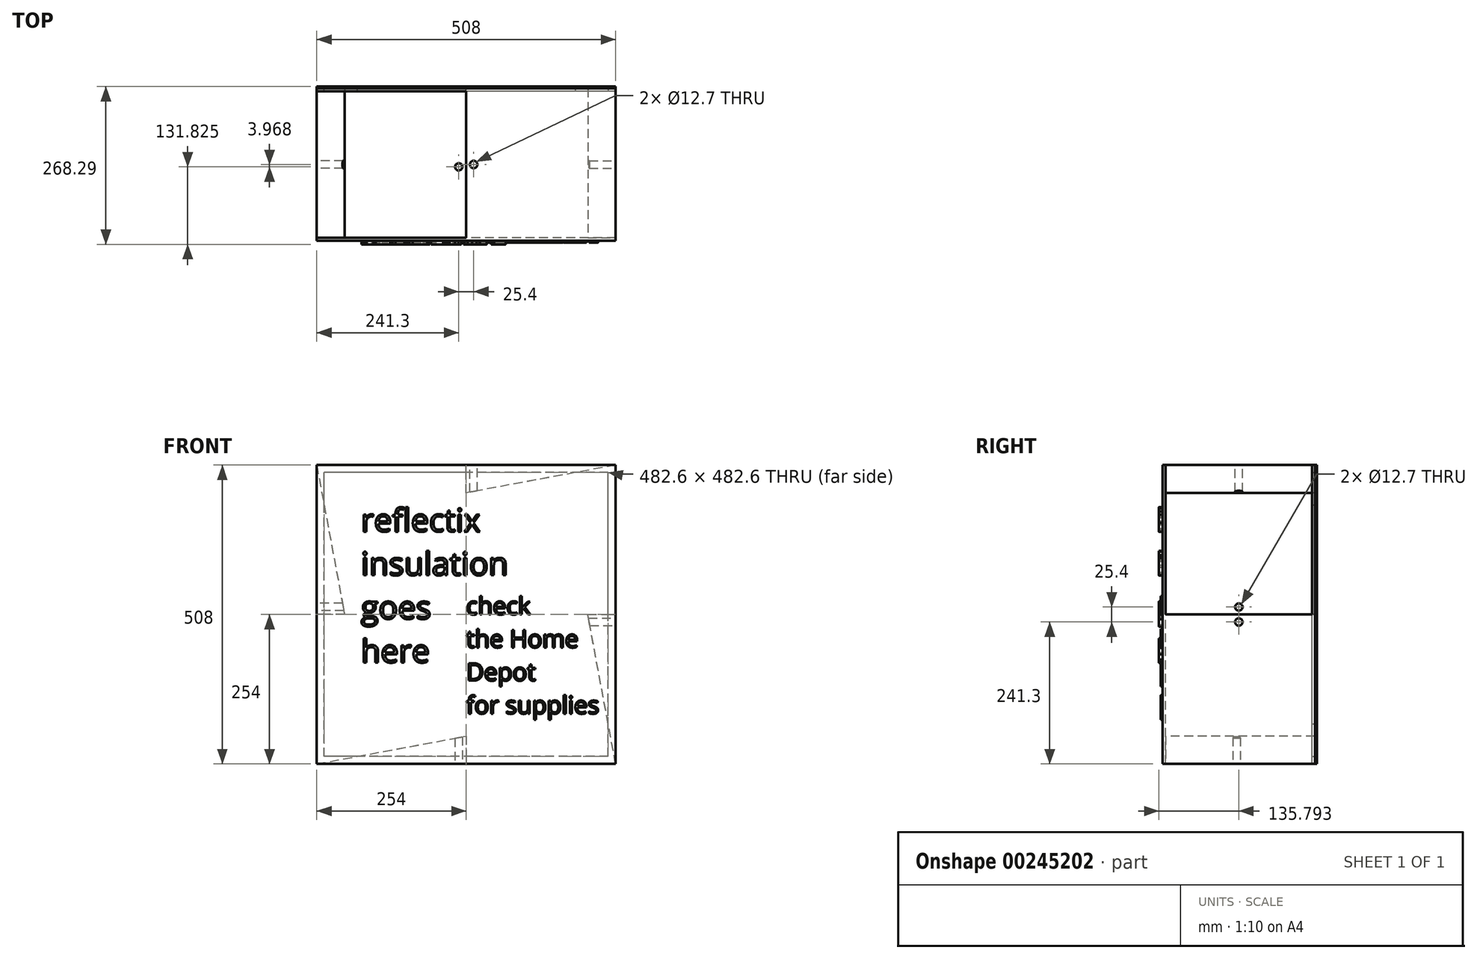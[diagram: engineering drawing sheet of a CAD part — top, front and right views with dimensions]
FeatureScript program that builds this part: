
annotation { "Feature Type Name" : "Feature", "Feature Type Description" : "" }
export const myFeature = defineFeature(function(context is Context, id is Id, definition is map)
    precondition{}
    {
        {
            var Q0;
            Q0=qCreatedBy(makeId("Front.planeOp"),FACE);
            var sketch = newSketch(context, id + "F0", { "sketchPlane" : qUnion([Q0])});
            skLineSegment(sketch, "E0.bottom", {"start": v(254, -254) * mm, "end": v(-254, -254) * mm});
            skLineSegment(sketch, "E0.top", {"start": v(254, 254) * mm, "end": v(-254, 254) * mm});
            skLineSegment(sketch, "E0.left", {"start": v(254, -254) * mm, "end": v(254, 254) * mm});
            skLineSegment(sketch, "E0.right", {"start": v(-254, -254) * mm, "end": v(-254, 254) * mm});
            skPoint(sketch, "E0.middle", {"position": v(0, 0) * mm});
            skSolve(sketch);
        }
        {
            var Q0;
            Q0=makeQuery(id+"F0.imprint","IMPRINT",FACE,{"disambiguationData":[TD([[makeQuery(id+"F0.imprint","IMPRINT",EDGE,{"derivedFrom":sQuery(id+"F0.wireOp",EDGE,"E0.bottom")}),-1.0]])]});
            extrude(context, id + "F1", {"entities" : qUnion([Q0]), "endBound" : BoundingType.SYMMETRIC, "depth" : 4.76 * mm});
        }
        {
            var Q0;
            Q0=makeQuery(id+"F1.opExtrude","CAP_FACE",FACE,{"disambiguationData":[OSD([sQuery(id+"F0.wireOp",EDGE,"E0.bottom"),sQuery(id+"F0.wireOp",EDGE,"E0.top"),sQuery(id+"F0.wireOp",EDGE,"E0.left"),sQuery(id+"F0.wireOp",EDGE,"E0.right")])],"isStart":false});
            var sketch = newSketch(context, id + "F2", { "sketchPlane" : qUnion([Q0])});
            skLineSegment(sketch, "E1", {"start": v(-254, 254) * mm, "end": v(-206.7, 0) * mm});
            skLineSegment(sketch, "E2", {"start": v(-254, -254) * mm, "end": v(0, -206.7) * mm});
            skLineSegment(sketch, "E3", {"start": v(254, -254) * mm, "end": v(206.7, 0) * mm});
            skPoint(sketch, "E3.endSnap0", {"position": v(254, 0) * mm});
            skLineSegment(sketch, "E4", {"start": v(254, 254) * mm, "end": v(0, 206.7) * mm});
            skLineSegment(sketch, "E5", {"start": v(0, 206.7) * mm, "end": v(0, 254) * mm});
            skLineSegment(sketch, "E6", {"start": v(0, 254) * mm, "end": v(254, 254) * mm});
            skLineSegment(sketch, "E7", {"start": v(206.7, 0) * mm, "end": v(254, 0) * mm});
            skLineSegment(sketch, "E8", {"start": v(254, 0) * mm, "end": v(254, -254) * mm});
            skLineSegment(sketch, "E9", {"start": v(0, -206.7) * mm, "end": v(0, -254) * mm});
            skLineSegment(sketch, "E10", {"start": v(0, -254) * mm, "end": v(-254, -254) * mm});
            skLineSegment(sketch, "E11", {"start": v(-206.7, 0) * mm, "end": v(-254, 0) * mm});
            skLineSegment(sketch, "E12", {"start": v(-254, 0) * mm, "end": v(-254, 254) * mm});
            skSolve(sketch);
        }
        {
            var Q0;
            Q0=makeQuery(id+"F2.imprint","IMPRINT",FACE,{"disambiguationData":[TD([[makeQuery(id+"F2.imprint","IMPRINT",EDGE,{"derivedFrom":sQuery(id+"F2.wireOp",EDGE,"E3")}),-1.0]])]});
            var Q1;
            Q1=makeQuery(id+"F2.imprint","IMPRINT",FACE,{"disambiguationData":[TD([[makeQuery(id+"F2.imprint","IMPRINT",EDGE,{"derivedFrom":sQuery(id+"F2.wireOp",EDGE,"E2")}),-1.0]])]});
            var Q2;
            Q2=makeQuery(id+"F2.imprint","IMPRINT",FACE,{"disambiguationData":[TD([[makeQuery(id+"F2.imprint","IMPRINT",EDGE,{"derivedFrom":sQuery(id+"F2.wireOp",EDGE,"E1")}),-1.0]])]});
            var Q3;
            Q3=makeQuery(id+"F2.imprint","IMPRINT",FACE,{"disambiguationData":[TD([[makeQuery(id+"F2.imprint","IMPRINT",EDGE,{"derivedFrom":sQuery(id+"F2.wireOp",EDGE,"E4")}),-1.0]])]});
            extrude(context, id + "F3", {"entities" : qUnion([Q0, Q1, Q2, Q3]), "operationType" : NewBodyOperationType.ADD, "oppositeDirection" : true, "depth" : 258.76 * mm});
        }
        {
            var Q0;
            Q0=makeQuery(id+"F1.opExtrude","CAP_FACE",FACE,{"disambiguationData":[OSD([sQuery(id+"F0.wireOp",EDGE,"E0.bottom"),sQuery(id+"F0.wireOp",EDGE,"E0.top"),sQuery(id+"F0.wireOp",EDGE,"E0.left"),sQuery(id+"F0.wireOp",EDGE,"E0.right")])],"isStart":false});
            var sketch = newSketch(context, id + "F4", { "sketchPlane" : qUnion([Q0])});
            skText(sketch, "E13", { "text": "reflectix\ninsulation\ngoes\nhere", "fontName": "OpenSans-Regular.ttf"});
            const initialGuessF4  = {"E13": [-0.17887, 0.14085, 1, 0, 0.03926]};
            skSetInitialGuess(sketch, initialGuessF4);
            skSolve(sketch);
        }
        {
            var Q0;
            Q0 = qSketchRegion(id + "F4", true);
            extrude(context, id + "F5", {"entities" : qUnion([Q0]), "operationType" : NewBodyOperationType.ADD, "depth" : 6.35 * mm});
        }
        {
            var Q0;
            {var subQ0=sQuery(id+"F0.wireOp",EDGE,"E0.bottom");var subQ1=sQuery(id+"F0.wireOp",EDGE,"E0.top");var subQ2=sQuery(id+"F0.wireOp",EDGE,"E0.left");var subQ3=sQuery(id+"F0.wireOp",EDGE,"E0.right");Q0=makeQuery(id+"F5.boolean.opBoolean","SPLIT",FACE,{"disambiguationData":[TD([makeQuery(id+"F1.opExtrude","SWEPT_FACE",FACE,{"disambiguationData":[OSD([subQ0])]})])],"derivedFrom":makeQuery(id+"F1.opExtrude","CAP_FACE",FACE,{"disambiguationData":[OSD([subQ0,subQ1,subQ2,subQ3])],"isStart":false})});}
            var sketch = newSketch(context, id + "F6", { "sketchPlane" : qUnion([Q0])});
            skText(sketch, "E14", { "text": "check\nthe Home\nDepot\nfor supplies", "fontName": "OpenSans-Regular.ttf"});
            const initialGuessF6  = {"E14": [0, 0, 1, 0, 0.02975]};
            skSetInitialGuess(sketch, initialGuessF6);
            skSolve(sketch);
        }
        {
            var Q0;
            Q0 = qSketchRegion(id + "F6", true);
            extrude(context, id + "F7", {"entities" : qUnion([Q0]), "operationType" : NewBodyOperationType.ADD, "depth" : 3.17 * mm});
        }
        {
            var Q0;
            Q0=makeQuery(id+"F4.imprint","IMPRINT",FACE,{"disambiguationData":[TD([[makeQuery(id+"F4.imprint","IMPRINT",EDGE,{"derivedFrom":sQuery(id+"F4.wireOp",EDGE,"E13.sketch_text.stroke-0")}),1.0]])]});
            cPlane(context, id + "F8", {"entities" : qUnion([Q0]), "cplaneType" : CPlaneType.OFFSET, "offset" : 258.76 * mm, "oppositeDirection" : true, "width" : 152.4 * mm, "height" : 152.4 * mm});
        }
        {
            var Q0;
            Q0=qCreatedBy(id+"F8.planeOp",FACE);
            var sketch = newSketch(context, id + "F9", { "sketchPlane" : qUnion([Q0])});
            skLineSegment(sketch, "E15.bottom", {"start": v(254, -254) * mm, "end": v(-254, -254) * mm});
            skLineSegment(sketch, "E15.top", {"start": v(254, 254) * mm, "end": v(-254, 254) * mm});
            skLineSegment(sketch, "E15.left", {"start": v(254, -254) * mm, "end": v(254, 254) * mm});
            skLineSegment(sketch, "E15.right", {"start": v(-254, -254) * mm, "end": v(-254, 254) * mm});
            skPoint(sketch, "E15.middle", {"position": v(0, 0) * mm});
            skLineSegment(sketch, "E16.bottom", {"start": v(241.3, -241.3) * mm, "end": v(-241.3, -241.3) * mm});
            skLineSegment(sketch, "E16.top", {"start": v(241.3, 241.3) * mm, "end": v(-241.3, 241.3) * mm});
            skLineSegment(sketch, "E16.left", {"start": v(241.3, -241.3) * mm, "end": v(241.3, 241.3) * mm});
            skLineSegment(sketch, "E16.right", {"start": v(-241.3, -241.3) * mm, "end": v(-241.3, 241.3) * mm});
            skSolve(sketch);
        }
        {
            var Q0;
            Q0=makeQuery(id+"F9.imprint","IMPRINT",FACE,{"disambiguationData":[TD([[makeQuery(id+"F9.imprint","IMPRINT",EDGE,{"derivedFrom":sQuery(id+"F9.wireOp",EDGE,"E15.bottom")}),-1.0]])]});
            extrude(context, id + "F10", {"entities" : qUnion([Q0]), "depth" : 4.64 * mm});
        }
        {
            var Q0;
            Q0=makeQuery(id+"F10.opExtrude","CAP_FACE",FACE,{"disambiguationData":[OSD([sQuery(id+"F9.wireOp",EDGE,"E15.bottom"),sQuery(id+"F9.wireOp",EDGE,"E15.top"),sQuery(id+"F9.wireOp",EDGE,"E15.left"),sQuery(id+"F9.wireOp",EDGE,"E15.right"),sQuery(id+"F9.wireOp",EDGE,"E16.bottom"),sQuery(id+"F9.wireOp",EDGE,"E16.top"),sQuery(id+"F9.wireOp",EDGE,"E16.left"),sQuery(id+"F9.wireOp",EDGE,"E16.right")])],"isStart":true});
            extrude(context, id + "F11", {"entities" : qUnion([Q0]), "depth" : 3.17 * mm});
        }
        {
            var Q0;
            Q0=makeQuery(id+"F10.opExtrude","SWEPT_BODY",BODY,{"disambiguationData":[OSD([sQuery(id+"F9.wireOp",EDGE,"E15.bottom"),sQuery(id+"F9.wireOp",EDGE,"E15.top"),sQuery(id+"F9.wireOp",EDGE,"E15.left"),sQuery(id+"F9.wireOp",EDGE,"E15.right"),sQuery(id+"F9.wireOp",EDGE,"E16.bottom"),sQuery(id+"F9.wireOp",EDGE,"E16.top"),sQuery(id+"F9.wireOp",EDGE,"E16.left"),sQuery(id+"F9.wireOp",EDGE,"E16.right")])]});
            var Q1;
            Q1=makeQuery(id+"F1.opExtrude","SWEPT_BODY",BODY,{"disambiguationData":[OSD([sQuery(id+"F0.wireOp",EDGE,"E0.bottom"),sQuery(id+"F0.wireOp",EDGE,"E0.top"),sQuery(id+"F0.wireOp",EDGE,"E0.left"),sQuery(id+"F0.wireOp",EDGE,"E0.right")])]});
            booleanBodies(context, id + "F12", {"operationType" : BooleanOperationType.UNION, "tools" : qUnion([Q0, Q1])});
        }
        {
            var Q0;
            Q0=makeQuery(id+"F12.opBoolean","MERGE",FACE,{"derivedFrom":[makeQuery(id+"F3.boolean.opBoolean","MERGE",FACE,{"derivedFrom":[makeQuery(id+"F1.opExtrude","SWEPT_FACE",FACE,{"disambiguationData":[OSD([sQuery(id+"F0.wireOp",EDGE,"E0.right")])]}),makeQuery(id+"F3.opExtrude","SWEPT_FACE",FACE,{"disambiguationData":[OSD([sQuery(id+"F2.wireOp",EDGE,"E12")])]})]}),makeQuery(id+"F10.opExtrude","SWEPT_FACE",FACE,{"disambiguationData":[OSD([sQuery(id+"F9.wireOp",EDGE,"E15.right")])]})]});
            var sketch = newSketch(context, id + "F13", { "sketchPlane" : qUnion([Q0])});
            skCircle(sketch, "E17", {"center": v(-127.06, 12.7) * mm, "radius": 12.7 * mm});
            skCircle(sketch, "E18", {"center": v(-127.06, 12.7) * mm, "radius": 6.35 * mm});
            skSolve(sketch);
        }
        {
            var Q0;
            Q0=makeQuery(id+"F13.imprint","IMPRINT",FACE,{"disambiguationData":[TD([[makeQuery(id+"F13.imprint","IMPRINT",EDGE,{"derivedFrom":sQuery(id+"F13.wireOp",EDGE,"E18")}),1.0]])]});
            extrude(context, id + "F14", {"entities" : qUnion([Q0]), "operationType" : NewBodyOperationType.REMOVE, "endBound" : BoundingType.THROUGH_ALL, "oppositeDirection" : true, "depth" : 25.4 * mm});
        }
        {
            var Q0;
            Q0=makeQuery(id+"F12.opBoolean","MERGE",FACE,{"derivedFrom":[makeQuery(id+"F3.boolean.opBoolean","MERGE",FACE,{"derivedFrom":[makeQuery(id+"F1.opExtrude","SWEPT_FACE",FACE,{"disambiguationData":[OSD([sQuery(id+"F0.wireOp",EDGE,"E0.bottom")])]}),makeQuery(id+"F3.opExtrude","SWEPT_FACE",FACE,{"disambiguationData":[OSD([sQuery(id+"F2.wireOp",EDGE,"E10")])]})]}),makeQuery(id+"F10.opExtrude","SWEPT_FACE",FACE,{"disambiguationData":[OSD([sQuery(id+"F9.wireOp",EDGE,"E15.bottom")])]})]});
            var sketch = newSketch(context, id + "F15", { "sketchPlane" : qUnion([Q0])});
            skCircle(sketch, "E19", {"center": v(-12.7, -123.1) * mm, "radius": 12.7 * mm});
            skCircle(sketch, "E20", {"center": v(-12.7, -123.1) * mm, "radius": 6.35 * mm});
            skSolve(sketch);
        }
        {
            var Q0;
            Q0=makeQuery(id+"F15.imprint","IMPRINT",FACE,{"disambiguationData":[TD([[makeQuery(id+"F15.imprint","IMPRINT",EDGE,{"derivedFrom":sQuery(id+"F15.wireOp",EDGE,"E20")}),1.0]])]});
            extrude(context, id + "F16", {"entities" : qUnion([Q0]), "operationType" : NewBodyOperationType.REMOVE, "endBound" : BoundingType.THROUGH_ALL, "oppositeDirection" : true, "depth" : 25.4 * mm});
        }
        {
            var Q0;
            Q0=makeQuery(id+"F12.opBoolean","MERGE",FACE,{"derivedFrom":[makeQuery(id+"F3.boolean.opBoolean","MERGE",FACE,{"derivedFrom":[makeQuery(id+"F1.opExtrude","SWEPT_FACE",FACE,{"disambiguationData":[OSD([sQuery(id+"F0.wireOp",EDGE,"E0.left")])]}),makeQuery(id+"F3.opExtrude","SWEPT_FACE",FACE,{"disambiguationData":[OSD([sQuery(id+"F2.wireOp",EDGE,"E8")])]})]}),makeQuery(id+"F10.opExtrude","SWEPT_FACE",FACE,{"disambiguationData":[OSD([sQuery(id+"F9.wireOp",EDGE,"E15.left")])]})]});
            var sketch = newSketch(context, id + "F17", { "sketchPlane" : qUnion([Q0])});
            skCircle(sketch, "E21", {"center": v(127.06, -12.7) * mm, "radius": 6.35 * mm});
            skPoint(sketch, "E21.centerSnap0", {"position": v(127.06, 0) * mm});
            skLineSegment(sketch, "E22", {"start": v(127.06, 0) * mm, "end": v(127.06, -6.35) * mm});
            skSolve(sketch);
        }
        {
            var Q0;
            Q0=makeQuery(id+"F17.imprint","IMPRINT",FACE,{"disambiguationData":[TD([[makeQuery(id+"F17.imprint","IMPRINT",EDGE,{"derivedFrom":sQuery(id+"F17.wireOp",EDGE,"E21")}),1.0]])]});
            extrude(context, id + "F18", {"entities" : qUnion([Q0]), "operationType" : NewBodyOperationType.REMOVE, "endBound" : BoundingType.THROUGH_ALL, "oppositeDirection" : true, "depth" : 25.4 * mm});
        }
        {
            var Q0;
            Q0=makeQuery(id+"F12.opBoolean","MERGE",FACE,{"derivedFrom":[makeQuery(id+"F3.boolean.opBoolean","MERGE",FACE,{"derivedFrom":[makeQuery(id+"F1.opExtrude","SWEPT_FACE",FACE,{"disambiguationData":[OSD([sQuery(id+"F0.wireOp",EDGE,"E0.top")])]}),makeQuery(id+"F3.opExtrude","SWEPT_FACE",FACE,{"disambiguationData":[OSD([sQuery(id+"F2.wireOp",EDGE,"E6")])]})]}),makeQuery(id+"F10.opExtrude","SWEPT_FACE",FACE,{"disambiguationData":[OSD([sQuery(id+"F9.wireOp",EDGE,"E15.top")])]})]});
            var sketch = newSketch(context, id + "F19", { "sketchPlane" : qUnion([Q0])});
            skLineSegment(sketch, "E23", {"start": v(0, 127.06) * mm, "end": v(12.7, 127.06) * mm});
            skCircle(sketch, "E24", {"center": v(12.7, 127.06) * mm, "radius": 6.35 * mm});
            skSolve(sketch);
        }
        {
            var Q0;
            Q0=makeQuery(id+"F19.imprint","IMPRINT",FACE,{"disambiguationData":[TD([[makeQuery(id+"F19.imprint","IMPRINT",EDGE,{"derivedFrom":sQuery(id+"F19.wireOp",EDGE,"E24")}),1.0]])]});
            extrude(context, id + "F20", {"entities" : qUnion([Q0]), "operationType" : NewBodyOperationType.REMOVE, "endBound" : BoundingType.THROUGH_ALL, "oppositeDirection" : true, "depth" : 25.4 * mm});
        }
    });
